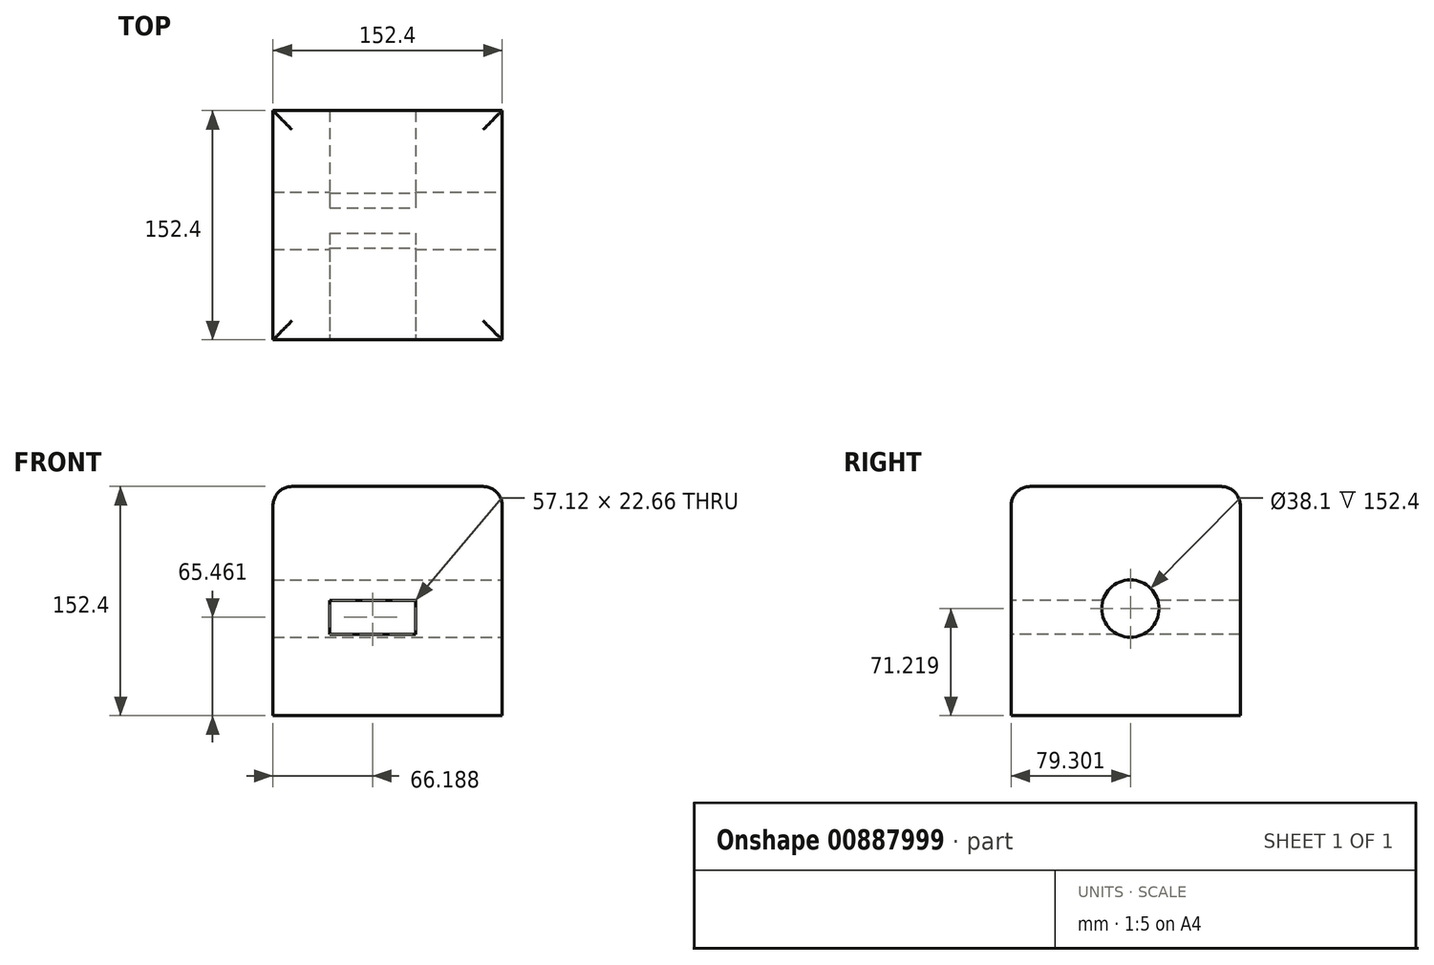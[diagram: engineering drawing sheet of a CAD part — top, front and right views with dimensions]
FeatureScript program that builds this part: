
annotation { "Feature Type Name" : "Feature", "Feature Type Description" : "" }
export const myFeature = defineFeature(function(context is Context, id is Id, definition is map)
    precondition{}
    {
        {
            var Q0;
            Q0=qCreatedBy(makeId("Front.planeOp"),FACE);
            var sketch = newSketch(context, id + "F0", { "sketchPlane" : qUnion([Q0])});
            skLineSegment(sketch, "E0.bottom", {"start": v(0, 0) * mm, "end": v(152.4, 0) * mm});
            skLineSegment(sketch, "E0.top", {"start": v(0, 152.4) * mm, "end": v(152.4, 152.4) * mm});
            skLineSegment(sketch, "E0.left", {"start": v(0, 0) * mm, "end": v(0, 152.4) * mm});
            skLineSegment(sketch, "E0.right", {"start": v(152.4, 0) * mm, "end": v(152.4, 152.4) * mm});
            skSolve(sketch);
        }
        {
            var Q0;
            Q0 = qSketchRegion(id + "F0", true);
            extrude(context, id + "F1", {"entities" : qUnion([Q0]), "depth" : 152.4 * mm, "offsetDistance" : 25.4 * mm});
        }
        {
            var Q0;
            Q0=makeQuery(id+"F1.opExtrude","CAP_EDGE",EDGE,{"disambiguationData":[OSD([sQuery(id+"F0.wireOp",EDGE,"E0.top")])],"isStart":false});
            var Q1;
            Q1=makeQuery(id+"F1.opExtrude","SWEPT_EDGE",EDGE,{"disambiguationData":[OSD([sQuery(id+"F0.wireOp",EDGE,"E0.top"),sQuery(id+"F0.wireOp",EDGE,"E0.left")])]});
            var Q2;
            Q2=makeQuery(id+"F1.opExtrude","CAP_EDGE",EDGE,{"disambiguationData":[OSD([sQuery(id+"F0.wireOp",EDGE,"E0.top")])],"isStart":true});
            var Q3;
            Q3=makeQuery(id+"F1.opExtrude","SWEPT_EDGE",EDGE,{"disambiguationData":[OSD([sQuery(id+"F0.wireOp",EDGE,"E0.top"),sQuery(id+"F0.wireOp",EDGE,"E0.right")])]});
            fillet(context, id + "F2", {"entities" : qUnion([Q0, Q1, Q2, Q3]), "radius" : 12.7 * mm, "tangentPropagation" : true, "allowEdgeOverflow" : false});
        }
        {
            var Q0;
            Q0=makeQuery(id+"F1.opExtrude","SWEPT_FACE",FACE,{"disambiguationData":[OSD([sQuery(id+"F0.wireOp",EDGE,"E0.right")])]});
            var sketch = newSketch(context, id + "F3", { "sketchPlane" : qUnion([Q0])});
            skPoint(sketch, "E1", {"position": v(-73.1, 71.22) * mm});
            skSolve(sketch);
        }
        {
            var Q0;
            Q0=sQuery(id+"F3.wireOp",VERTEX,"E1");
            var Q1;
            Q1=makeQuery(id+"F1.opExtrude","SWEPT_BODY",BODY,{"disambiguationData":[OSD([sQuery(id+"F0.wireOp",EDGE,"E0.bottom"),sQuery(id+"F0.wireOp",EDGE,"E0.top"),sQuery(id+"F0.wireOp",EDGE,"E0.left"),sQuery(id+"F0.wireOp",EDGE,"E0.right")])]});
            hole(context, id + "F4", {"style" : HoleStyle.SIMPLE, "endStyle" : HoleEndStyle.THROUGH, "holeDiameter" : 38.1 * mm, "majorDiameter" : 6.35 * mm, "isTappedThrough" : true, "tappedDepth" : 12.7 * mm, "tapClearance" : 3, "locations" : qUnion([Q0]), "scope" : qUnion([Q1])});
        }
        {
            var Q0;
            Q0=makeQuery(id+"F1.opExtrude","CAP_FACE",FACE,{"disambiguationData":[OSD([sQuery(id+"F0.wireOp",EDGE,"E0.bottom"),sQuery(id+"F0.wireOp",EDGE,"E0.top"),sQuery(id+"F0.wireOp",EDGE,"E0.left"),sQuery(id+"F0.wireOp",EDGE,"E0.right")])],"isStart":false});
            var sketch = newSketch(context, id + "F5", { "sketchPlane" : qUnion([Q0])});
            skLineSegment(sketch, "E2.bottom", {"start": v(37.63, 76.79) * mm, "end": v(94.75, 76.79) * mm});
            skLineSegment(sketch, "E2.top", {"start": v(37.63, 54.13) * mm, "end": v(94.75, 54.13) * mm});
            skLineSegment(sketch, "E2.left", {"start": v(37.63, 76.79) * mm, "end": v(37.63, 54.13) * mm});
            skLineSegment(sketch, "E2.right", {"start": v(94.75, 76.79) * mm, "end": v(94.75, 54.13) * mm});
            skSolve(sketch);
        }
        {
            var Q0;
            Q0 = qSketchRegion(id + "F5", true);
            extrude(context, id + "F6", {"entities" : qUnion([Q0]), "operationType" : NewBodyOperationType.REMOVE, "endBound" : BoundingType.THROUGH_ALL, "oppositeDirection" : true, "depth" : 25.4 * mm, "offsetDistance" : 25.4 * mm});
        }
    });
